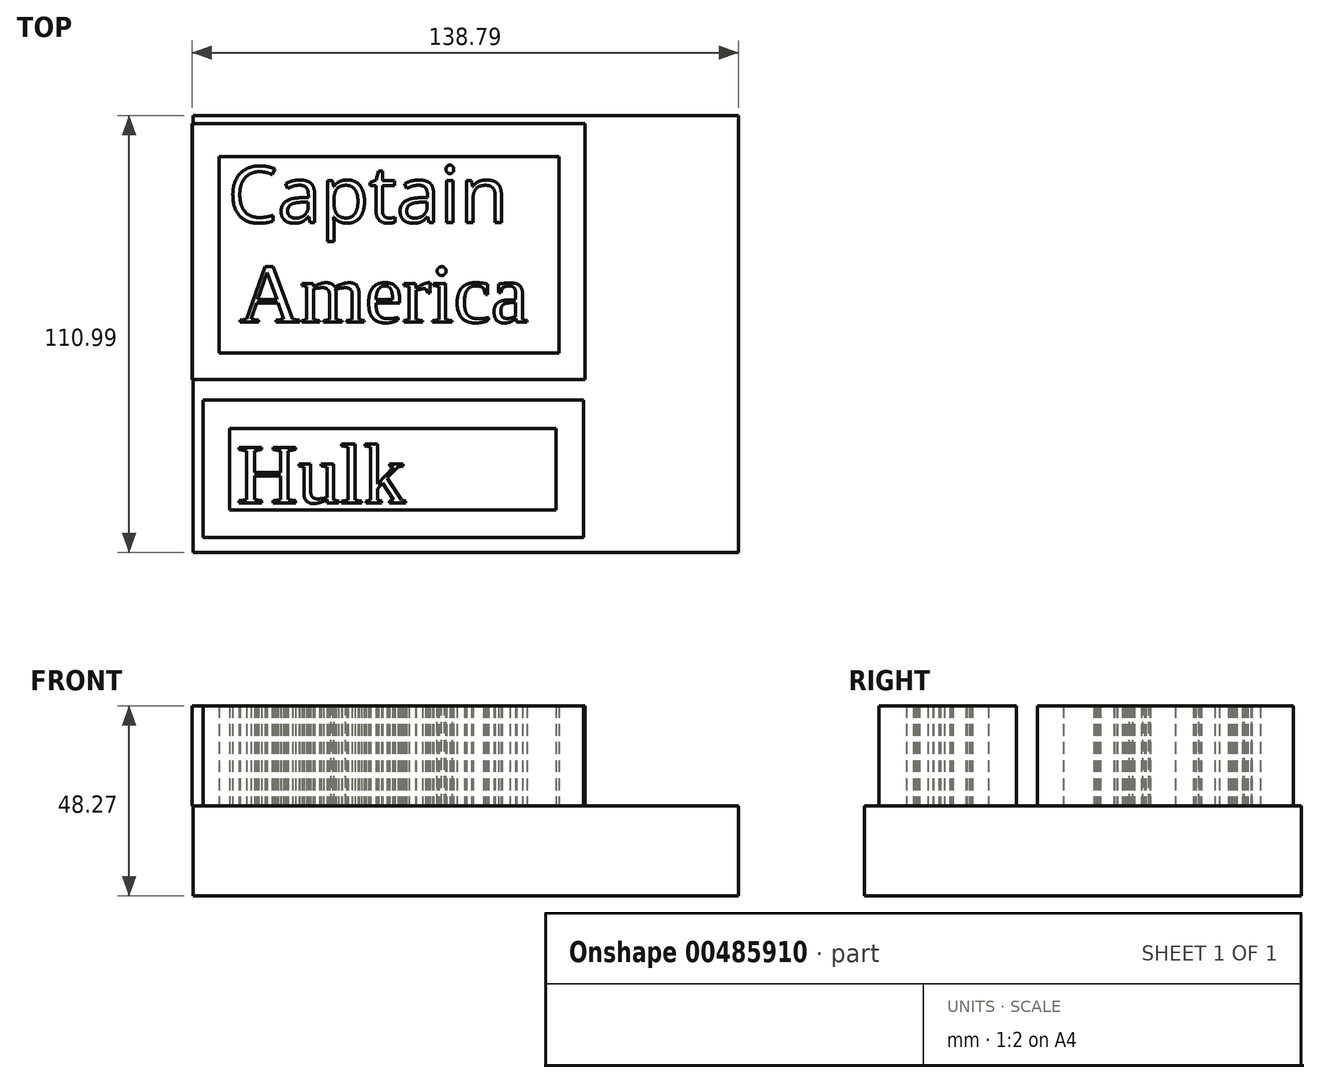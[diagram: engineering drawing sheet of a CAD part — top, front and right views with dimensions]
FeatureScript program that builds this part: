
annotation { "Feature Type Name" : "Feature", "Feature Type Description" : "" }
export const myFeature = defineFeature(function(context is Context, id is Id, definition is map)
    precondition{}
    {
        {
            var Q0;
            Q0=qCreatedBy(makeId("Top.planeOp"),FACE);
            var sketch = newSketch(context, id + "F0", { "sketchPlane" : qUnion([Q0])});
            skLineSegment(sketch, "E0.bottom", {"start": v(-66.39, 60.37) * mm, "end": v(72.2, 60.37) * mm});
            skLineSegment(sketch, "E0.top", {"start": v(-66.39, -50.62) * mm, "end": v(72.2, -50.62) * mm});
            skLineSegment(sketch, "E0.left", {"start": v(-66.39, 60.37) * mm, "end": v(-66.39, -50.62) * mm});
            skLineSegment(sketch, "E0.right", {"start": v(72.2, 60.37) * mm, "end": v(72.2, -50.62) * mm});
            skSolve(sketch);
        }
        {
            var Q0;
            Q0 = qSketchRegion(id + "F0", true);
            extrude(context, id + "F1", {"entities" : qUnion([Q0]), "depth" : 22.87 * mm});
        }
        {
            var Q0;
            Q0=makeQuery(id+"F1.opExtrude","CAP_FACE",FACE,{"disambiguationData":[OSD([sQuery(id+"F0.wireOp",EDGE,"E0.bottom"),sQuery(id+"F0.wireOp",EDGE,"E0.top"),sQuery(id+"F0.wireOp",EDGE,"E0.left"),sQuery(id+"F0.wireOp",EDGE,"E0.right")])],"isStart":false});
            var sketch = newSketch(context, id + "F2", { "sketchPlane" : qUnion([Q0])});
            skText(sketch, "E1", { "text": "Captain", "fontName": "OpenSans-Regular.ttf"});
            skText(sketch, "E2", { "text": "America", "fontName": "Tinos-Regular.ttf"});
            const initialGuessF2  = {"E1": [-0.05747, 0.0332, 1, 0, 0.01431], "E2": [-0.05456, 0.00788, 1, 0, 0.01535]};
            skSetInitialGuess(sketch, initialGuessF2);
            skSolve(sketch);
        }
        {
            var Q0;
            Q0=makeQuery(id+"F2.imprint","IMPRINT",FACE,{"disambiguationData":[TD([[makeQuery(id+"F2.imprint","IMPRINT",EDGE,{"derivedFrom":sQuery(id+"F2.wireOp",EDGE,"E1.sketch_text.stroke-0")}),-1.0]])]});
            extrude(context, id + "F3", {"entities" : qUnion([Q0]), "operationType" : NewBodyOperationType.ADD, "depth" : 25.4 * mm});
        }
        {
            var Q0;
            Q0=makeQuery(id+"F2.imprint","IMPRINT",FACE,{"disambiguationData":[TD([[makeQuery(id+"F2.imprint","IMPRINT",EDGE,{"derivedFrom":sQuery(id+"F2.wireOp",EDGE,"E1.sketch_text.stroke-15")}),-1.0]])]});
            extrude(context, id + "F4", {"entities" : qUnion([Q0]), "operationType" : NewBodyOperationType.ADD, "depth" : 25.4 * mm});
        }
        {
            var Q0;
            Q0=makeQuery(id+"F2.imprint","IMPRINT",FACE,{"disambiguationData":[TD([[makeQuery(id+"F2.imprint","IMPRINT",EDGE,{"derivedFrom":sQuery(id+"F2.wireOp",EDGE,"E1.sketch_text.stroke-42")}),-1.0]])]});
            extrude(context, id + "F5", {"entities" : qUnion([Q0]), "operationType" : NewBodyOperationType.ADD, "depth" : 25.4 * mm});
        }
        {
            var Q0;
            Q0=makeQuery(id+"F2.imprint","IMPRINT",FACE,{"disambiguationData":[TD([[makeQuery(id+"F2.imprint","IMPRINT",EDGE,{"derivedFrom":sQuery(id+"F2.wireOp",EDGE,"E1.sketch_text.stroke-67")}),-1.0]])]});
            extrude(context, id + "F6", {"entities" : qUnion([Q0]), "operationType" : NewBodyOperationType.ADD, "depth" : 25.4 * mm});
        }
        {
            var Q0;
            Q0=makeQuery(id+"F2.imprint","IMPRINT",FACE,{"disambiguationData":[TD([[makeQuery(id+"F2.imprint","IMPRINT",EDGE,{"derivedFrom":sQuery(id+"F2.wireOp",EDGE,"E1.sketch_text.stroke-86")}),-1.0]])]});
            extrude(context, id + "F7", {"entities" : qUnion([Q0]), "operationType" : NewBodyOperationType.ADD, "depth" : 25.4 * mm});
        }
        {
            var Q0;
            Q0=makeQuery(id+"F2.imprint","IMPRINT",FACE,{"disambiguationData":[TD([[makeQuery(id+"F2.imprint","IMPRINT",EDGE,{"derivedFrom":sQuery(id+"F2.wireOp",EDGE,"E1.sketch_text.stroke-117")}),-1.0]])]});
            var Q1;
            Q1=makeQuery(id+"F2.imprint","IMPRINT",FACE,{"disambiguationData":[TD([[makeQuery(id+"F2.imprint","IMPRINT",EDGE,{"derivedFrom":sQuery(id+"F2.wireOp",EDGE,"E1.sketch_text.stroke-113")}),-1.0]])]});
            extrude(context, id + "F8", {"entities" : qUnion([Q0, Q1]), "operationType" : NewBodyOperationType.ADD, "depth" : 25.4 * mm});
        }
        {
            var Q0;
            Q0=makeQuery(id+"F2.imprint","IMPRINT",FACE,{"disambiguationData":[TD([[makeQuery(id+"F2.imprint","IMPRINT",EDGE,{"derivedFrom":sQuery(id+"F2.wireOp",EDGE,"E1.sketch_text.stroke-125")}),-1.0]])]});
            extrude(context, id + "F9", {"entities" : qUnion([Q0]), "operationType" : NewBodyOperationType.ADD, "depth" : 25.4 * mm});
        }
        {
            var Q0;
            Q0=makeQuery(id+"F2.imprint","IMPRINT",FACE,{"disambiguationData":[TD([[makeQuery(id+"F2.imprint","IMPRINT",EDGE,{"derivedFrom":sQuery(id+"F2.wireOp",EDGE,"E2.sketch_text.stroke-0")}),-1.0]])]});
            var Q1;
            Q1=makeQuery(id+"F2.imprint","IMPRINT",FACE,{"disambiguationData":[TD([[makeQuery(id+"F2.imprint","IMPRINT",EDGE,{"derivedFrom":sQuery(id+"F2.wireOp",EDGE,"E2.sketch_text.stroke-19")}),-1.0]])]});
            var Q2;
            Q2=makeQuery(id+"F2.imprint","IMPRINT",FACE,{"disambiguationData":[TD([[makeQuery(id+"F2.imprint","IMPRINT",EDGE,{"derivedFrom":sQuery(id+"F2.wireOp",EDGE,"E2.sketch_text.stroke-60")}),-1.0]])]});
            var Q3;
            Q3=makeQuery(id+"F2.imprint","IMPRINT",FACE,{"disambiguationData":[TD([[makeQuery(id+"F2.imprint","IMPRINT",EDGE,{"derivedFrom":sQuery(id+"F2.wireOp",EDGE,"E2.sketch_text.stroke-81")}),-1.0]])]});
            var Q4;
            Q4=makeQuery(id+"F2.imprint","IMPRINT",FACE,{"disambiguationData":[TD([[makeQuery(id+"F2.imprint","IMPRINT",EDGE,{"derivedFrom":sQuery(id+"F2.wireOp",EDGE,"E2.sketch_text.stroke-108")}),-1.0]])]});
            extrude(context, id + "F10", {"entities" : qUnion([Q0, Q1, Q2, Q3, Q4]), "operationType" : NewBodyOperationType.ADD, "depth" : 25.4 * mm});
        }
        {
            var Q0;
            Q0=makeQuery(id+"F2.imprint","IMPRINT",FACE,{"disambiguationData":[TD([[makeQuery(id+"F2.imprint","IMPRINT",EDGE,{"derivedFrom":sQuery(id+"F2.wireOp",EDGE,"E2.sketch_text.stroke-100")}),-1.0]])]});
            var Q1;
            Q1=makeQuery(id+"F2.imprint","IMPRINT",FACE,{"disambiguationData":[TD([[makeQuery(id+"F2.imprint","IMPRINT",EDGE,{"derivedFrom":sQuery(id+"F2.wireOp",EDGE,"E2.sketch_text.stroke-118")}),-1.0]])]});
            var Q2;
            Q2=makeQuery(id+"F2.imprint","IMPRINT",FACE,{"disambiguationData":[TD([[makeQuery(id+"F2.imprint","IMPRINT",EDGE,{"derivedFrom":sQuery(id+"F2.wireOp",EDGE,"E2.sketch_text.stroke-133")}),-1.0]])]});
            extrude(context, id + "F11", {"entities" : qUnion([Q0, Q1, Q2]), "operationType" : NewBodyOperationType.ADD, "depth" : 25.4 * mm});
        }
        {
            var Q0;
            Q0=makeQuery(id+"F2.imprint","IMPRINT",FACE,{"disambiguationData":[TD([[makeQuery(id+"F2.imprint","IMPRINT",EDGE,{"derivedFrom":sQuery(id+"F2.wireOp",EDGE,"E1.sketch_text.stroke-0")}),1.0]])]});
            var sketch = newSketch(context, id + "F12", { "sketchPlane" : qUnion([Q0])});
            skLineSegment(sketch, "E3.bottom", {"start": v(-59.75, 50) * mm, "end": v(26.55, 50) * mm});
            skLineSegment(sketch, "E3.top", {"start": v(-59.75, 0) * mm, "end": v(26.55, 0) * mm});
            skLineSegment(sketch, "E3.left", {"start": v(-59.75, 50) * mm, "end": v(-59.75, 0) * mm});
            skLineSegment(sketch, "E3.right", {"start": v(26.55, 50) * mm, "end": v(26.55, 0) * mm});
            skLineSegment(sketch, "E4.bottom", {"start": v(33.2, -6.64) * mm, "end": v(-66.6, -6.64) * mm});
            skLineSegment(sketch, "E4.top", {"start": v(33.2, 58.3) * mm, "end": v(-66.6, 58.3) * mm});
            skLineSegment(sketch, "E4.left", {"start": v(33.2, -6.64) * mm, "end": v(33.2, 58.3) * mm});
            skLineSegment(sketch, "E4.right", {"start": v(-66.6, -6.64) * mm, "end": v(-66.6, 58.3) * mm});
            skSolve(sketch);
        }
        {
            var Q0;
            Q0 = qSketchRegion(id + "F12", true);
            extrude(context, id + "F13", {"entities" : qUnion([Q0]), "operationType" : NewBodyOperationType.ADD, "depth" : 25.4 * mm});
        }
        {
            var Q0;
            Q0=makeQuery(id+"F2.imprint","IMPRINT",FACE,{"disambiguationData":[TD([[makeQuery(id+"F2.imprint","IMPRINT",EDGE,{"derivedFrom":sQuery(id+"F2.wireOp",EDGE,"E1.sketch_text.stroke-0")}),1.0]])]});
            var sketch = newSketch(context, id + "F14", { "sketchPlane" : qUnion([Q0])});
            skLineSegment(sketch, "E5.bottom", {"start": v(-63.8, -11.94) * mm, "end": v(32.82, -11.94) * mm});
            skLineSegment(sketch, "E5.top", {"start": v(-63.8, -46.88) * mm, "end": v(32.82, -46.88) * mm});
            skLineSegment(sketch, "E5.left", {"start": v(-63.8, -11.94) * mm, "end": v(-63.8, -46.88) * mm});
            skLineSegment(sketch, "E5.right", {"start": v(32.82, -11.94) * mm, "end": v(32.82, -46.88) * mm});
            skLineSegment(sketch, "E6.bottom", {"start": v(-57.02, -19.15) * mm, "end": v(25.85, -19.15) * mm});
            skLineSegment(sketch, "E6.top", {"start": v(-57.02, -39.9) * mm, "end": v(25.85, -39.9) * mm});
            skLineSegment(sketch, "E6.left", {"start": v(-57.02, -19.15) * mm, "end": v(-57.02, -39.9) * mm});
            skLineSegment(sketch, "E6.right", {"start": v(25.85, -19.15) * mm, "end": v(25.85, -39.9) * mm});
            skSolve(sketch);
        }
        {
            var Q0;
            Q0 = qSketchRegion(id + "F14", true);
            extrude(context, id + "F15", {"entities" : qUnion([Q0]), "operationType" : NewBodyOperationType.ADD, "depth" : 25.4 * mm});
        }
        {
            var Q0;
            Q0=makeQuery(id+"F2.imprint","IMPRINT",FACE,{"disambiguationData":[TD([[makeQuery(id+"F2.imprint","IMPRINT",EDGE,{"derivedFrom":sQuery(id+"F2.wireOp",EDGE,"E1.sketch_text.stroke-0")}),1.0]])]});
            var sketch = newSketch(context, id + "F16", { "sketchPlane" : qUnion([Q0])});
            skText(sketch, "E7", { "text": "Hulk", "fontName": "Tinos-Regular.ttf"});
            const initialGuessF16  = {"E7": [-0.05522, -0.038, 1, 0, 0.01543]};
            skSetInitialGuess(sketch, initialGuessF16);
            skSolve(sketch);
        }
        {
            var Q0;
            Q0 = qSketchRegion(id + "F16", true);
            extrude(context, id + "F17", {"entities" : qUnion([Q0]), "operationType" : NewBodyOperationType.ADD, "depth" : 25.4 * mm});
        }
    });
